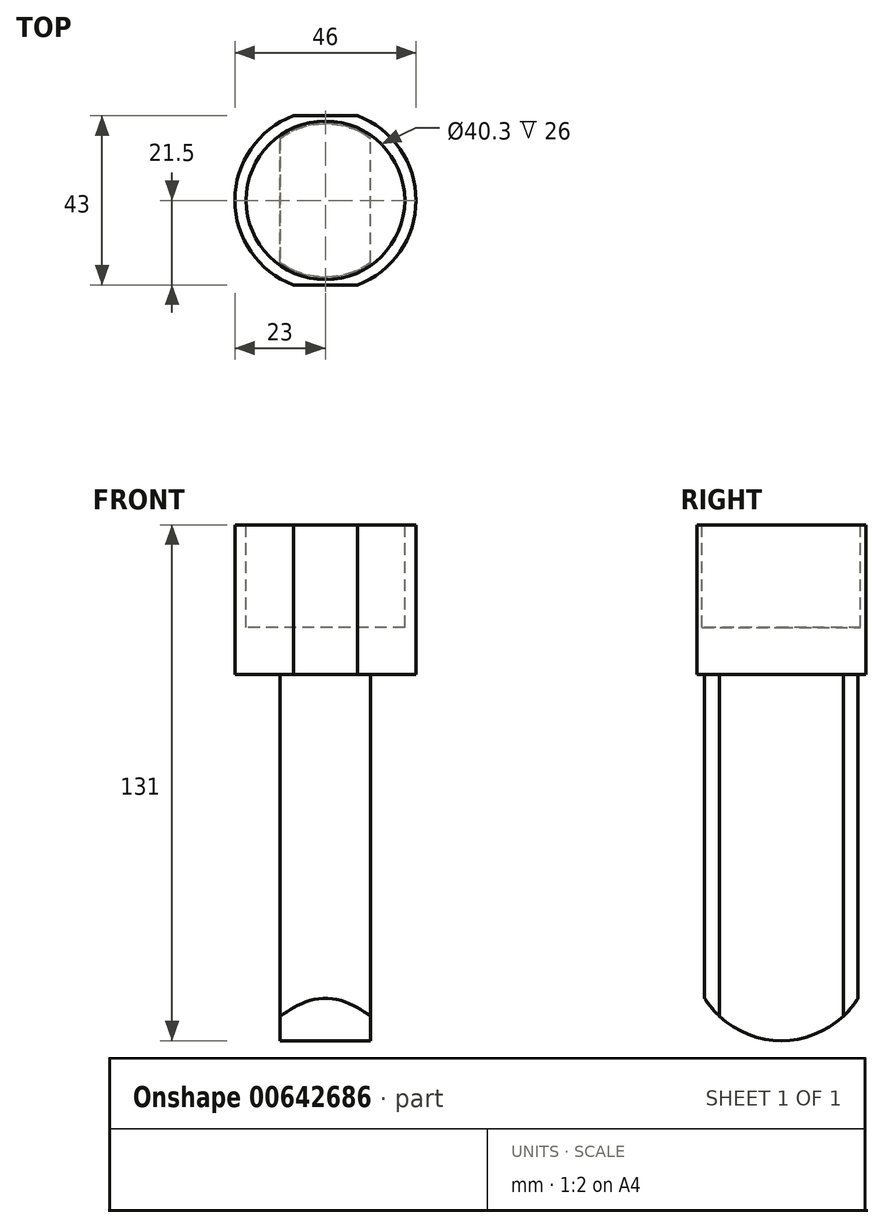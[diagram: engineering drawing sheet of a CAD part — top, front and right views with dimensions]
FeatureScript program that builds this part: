
annotation { "Feature Type Name" : "Feature", "Feature Type Description" : "" }
export const myFeature = defineFeature(function(context is Context, id is Id, definition is map)
    precondition{}
    {
        {
            var Q0;
            Q0=qCreatedBy(makeId("Top.planeOp"),FACE);
            var sketch = newSketch(context, id + "F0", { "sketchPlane" : qUnion([Q0])});
            skArc(sketch, "E0", {"start": v(-8.17, 21.5) * mm, "mid": v(-23, 0) * mm, "end": v(-8.17, -21.5) * mm});
            skLineSegment(sketch, "E1", {"start": v(-8.17, 21.5) * mm, "end": v(8.17, 21.5) * mm});
            skLineSegment(sketch, "E2.MirrorCS", {"start": v(-8.17, -21.5) * mm, "end": v(8.17, -21.5) * mm});
            skArc(sketch, "E3.trimOffspring", {"start": v(8.17, -21.5) * mm, "mid": v(23, 0) * mm, "end": v(8.17, 21.5) * mm});
            skSolve(sketch);
        }
        {
            var Q0;
            Q0 = qSketchRegion(id + "F0", true);
            extrude(context, id + "F1", {"entities" : qUnion([Q0]), "depth" : 38 * mm, "offsetDistance" : 25 * mm});
        }
        {
            var Q0;
            Q0=makeQuery(id+"F1.opExtrude","CAP_FACE",FACE,{"disambiguationData":[OSD([sQuery(id+"F0.wireOp",EDGE,"E0"),sQuery(id+"F0.wireOp",EDGE,"E1"),sQuery(id+"F0.wireOp",EDGE,"E2.MirrorCS"),sQuery(id+"F0.wireOp",EDGE,"E3.trimOffspring")])],"isStart":false});
            var sketch = newSketch(context, id + "F2", { "sketchPlane" : qUnion([Q0])});
            skCircle(sketch, "E4", {"center": v(0, 0) * mm, "radius": 20.15 * mm});
            skSolve(sketch);
        }
        {
            var Q0;
            Q0=makeQuery(id+"F2.imprint","IMPRINT",FACE,{"disambiguationData":[TD([[makeQuery(id+"F2.imprint","IMPRINT",EDGE,{"derivedFrom":sQuery(id+"F2.wireOp",EDGE,"E4")}),1.0]])]});
            extrude(context, id + "F3", {"entities" : qUnion([Q0]), "operationType" : NewBodyOperationType.REMOVE, "oppositeDirection" : true, "depth" : 26 * mm, "offsetDistance" : 25 * mm});
        }
        {
            var Q0;
            Q0=makeQuery(id+"F1.opExtrude","CAP_FACE",FACE,{"disambiguationData":[OSD([sQuery(id+"F0.wireOp",EDGE,"E0"),sQuery(id+"F0.wireOp",EDGE,"E1"),sQuery(id+"F0.wireOp",EDGE,"E2.MirrorCS"),sQuery(id+"F0.wireOp",EDGE,"E3.trimOffspring")])],"isStart":true});
            var sketch = newSketch(context, id + "F4", { "sketchPlane" : qUnion([Q0])});
            skArc(sketch, "E5", {"start": v(11.5, 15.75) * mm, "mid": v(0, 19.5) * mm, "end": v(-11.5, 15.75) * mm});
            skLineSegment(sketch, "E6", {"start": v(-11.5, 15.75) * mm, "end": v(-11.5, -15.75) * mm});
            skLineSegment(sketch, "E7.MirrorCS", {"start": v(11.5, 15.75) * mm, "end": v(11.5, -15.75) * mm});
            skArc(sketch, "E8.trimOffspring", {"start": v(-11.5, -15.75) * mm, "mid": v(0, -19.5) * mm, "end": v(11.5, -15.75) * mm});
            skSolve(sketch);
        }
        {
            var Q0;
            Q0=makeQuery(id+"F4.imprint","IMPRINT",FACE,{"disambiguationData":[TD([[makeQuery(id+"F4.imprint","IMPRINT",EDGE,{"derivedFrom":sQuery(id+"F4.wireOp",EDGE,"E5")}),1.0]])]});
            extrude(context, id + "F5", {"entities" : qUnion([Q0]), "operationType" : NewBodyOperationType.ADD, "depth" : 93 * mm, "offsetDistance" : 25 * mm});
        }
        {
            var Q0;
            Q0=makeQuery(id+"F5.opExtrude","SWEPT_FACE",FACE,{"disambiguationData":[OSD([sQuery(id+"F4.wireOp",EDGE,"E6")])]});
            var sketch = newSketch(context, id + "F6", { "sketchPlane" : qUnion([Q0])});
            skArc(sketch, "E9", {"start": v(-22.67, -73.89) * mm, "mid": v(2.07, -92.9) * mm, "end": v(23, -69.77) * mm});
            skLineSegment(sketch, "E10", {"start": v(-22.67, -73.89) * mm, "end": v(-27.42, -95.71) * mm});
            skLineSegment(sketch, "E11", {"start": v(-27.42, -95.71) * mm, "end": v(39.85, -95.71) * mm});
            skLineSegment(sketch, "E12", {"start": v(39.85, -95.71) * mm, "end": v(23, -69.77) * mm});
            skSolve(sketch);
        }
        {
            var Q0;
            {var subQ0=sQuery(id+"F6.wireOp",EDGE,"E9");var subQ1=sQuery(id+"F4.wireOp",EDGE,"E6");var subQ4=makeQuery(id+"F5.opExtrude","CAP_EDGE",EDGE,{"disambiguationData":[OSD([subQ1])],"isStart":false});var subQ5=makeQuery(id+"F6.imprint","INTERSECT",VERTEX,{"derivedFrom":[subQ4,subQ0]});Q0=makeQuery(id+"F6.imprint","IMPRINT",FACE,{"disambiguationData":[TD([[makeQuery(id+"F6.imprint","IMPRINT",EDGE,{"disambiguationData":[TD([[subQ5,1.0]])],"derivedFrom":subQ0}),-1.0]])]});}
            var Q1;
            {var subQ0=sQuery(id+"F6.wireOp",EDGE,"E9");var subQ1=sQuery(id+"F4.wireOp",EDGE,"E6");var subQ4=makeQuery(id+"F5.opExtrude","CAP_EDGE",EDGE,{"disambiguationData":[OSD([subQ1])],"isStart":false});var subQ5=makeQuery(id+"F6.imprint","INTERSECT",VERTEX,{"derivedFrom":[subQ4,subQ0]});Q1=makeQuery(id+"F6.imprint","IMPRINT",FACE,{"disambiguationData":[TD([[makeQuery(id+"F6.imprint","IMPRINT",EDGE,{"disambiguationData":[TD([[subQ5,-1.0]])],"derivedFrom":subQ0}),-1.0]])]});}
            var Q2;
            {var subQ0=sQuery(id+"F6.wireOp",EDGE,"E10");Q2=makeQuery(id+"F6.imprint","IMPRINT",FACE,{"disambiguationData":[TD([[makeQuery(id+"F6.imprint","IMPRINT",EDGE,{"derivedFrom":subQ0}),1.0]])]});}
            extrude(context, id + "F7", {"entities" : qUnion([Q0, Q1, Q2]), "operationType" : NewBodyOperationType.REMOVE, "oppositeDirection" : true, "depth" : 25 * mm, "offsetDistance" : 25 * mm});
        }
    });
